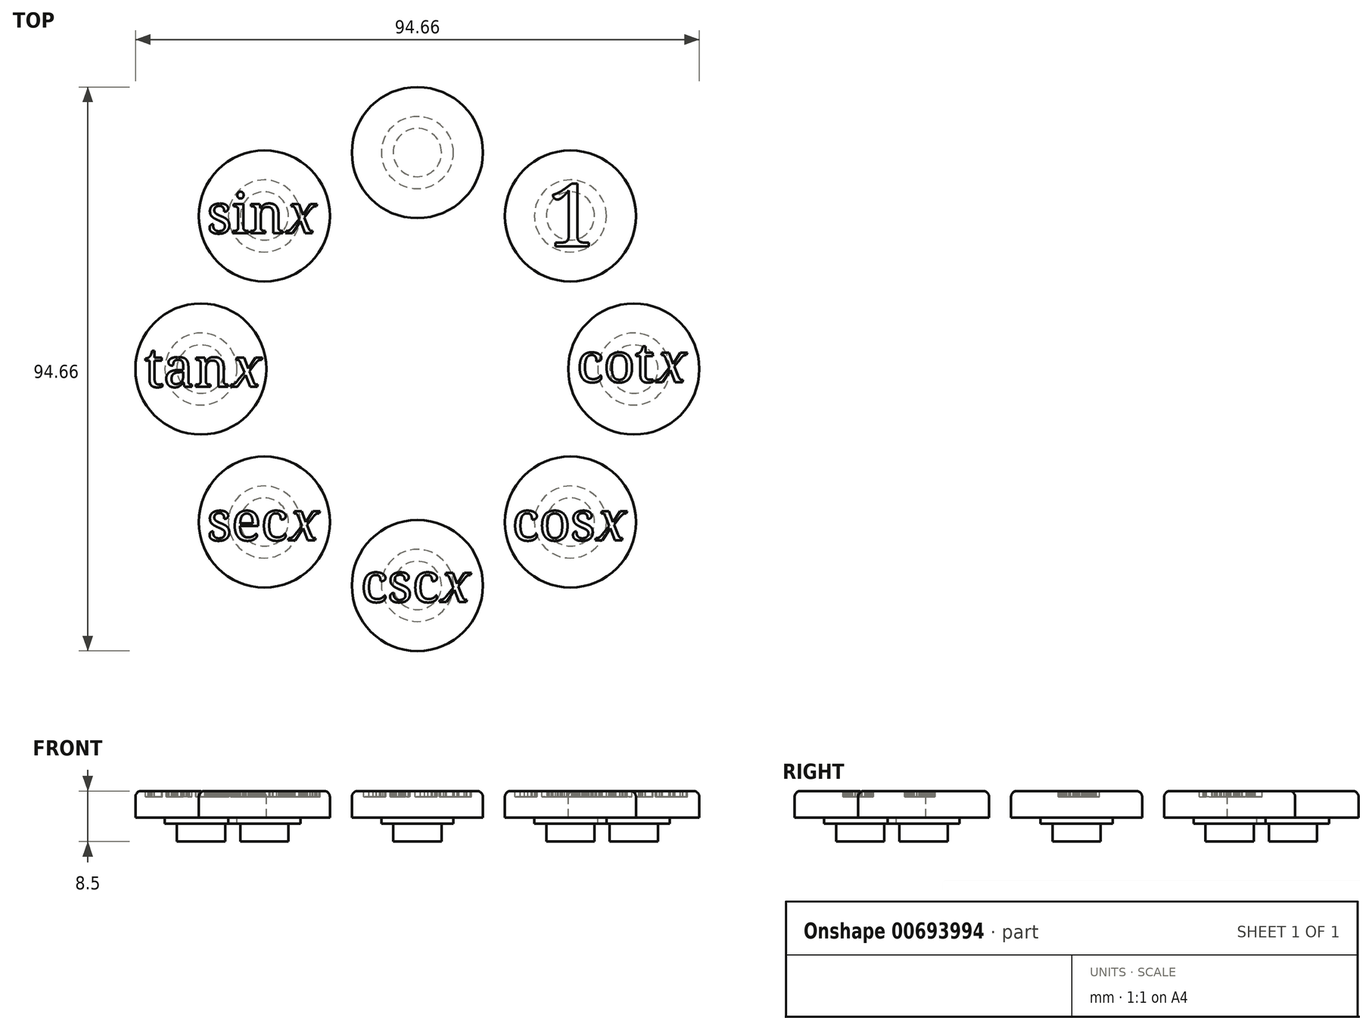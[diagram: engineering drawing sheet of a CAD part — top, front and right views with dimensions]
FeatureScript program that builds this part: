
annotation { "Feature Type Name" : "Feature", "Feature Type Description" : "" }
export const myFeature = defineFeature(function(context is Context, id is Id, definition is map)
    precondition{}
    {
        {
            var Q0;
            Q0=qCreatedBy(makeId("Top.planeOp"),FACE);
            var sketch = newSketch(context, id + "F0", { "sketchPlane" : qUnion([Q0])});
            skCircle(sketch, "E0", {"center": v(0, 0) * mm, "radius": 11 * mm});
            skCircle(sketch, "E1.0", {"center": v(0, 0) * mm, "radius": 4.05 * mm});
            skCircle(sketch, "E2.0", {"center": v(0, 0) * mm, "radius": 6.05 * mm});
            skSolve(sketch);
        }
        {
            var Q0;
            Q0=makeQuery(id+"F0.imprint","IMPRINT",FACE,{"disambiguationData":[TD([[makeQuery(id+"F0.imprint","IMPRINT",EDGE,{"derivedFrom":sQuery(id+"F0.wireOp",EDGE,"E0")}),1.0]])]});
            extrude(context, id + "F1", {"entities" : qUnion([Q0]), "depth" : 4.5 * mm, "offsetDistance" : 25.4 * mm});
        }
        {
            var Q0;
            Q0=makeQuery(id+"F0.imprint","IMPRINT",FACE,{"disambiguationData":[TD([[makeQuery(id+"F0.imprint","IMPRINT",EDGE,{"derivedFrom":sQuery(id+"F0.wireOp",EDGE,"E1.0")}),1.0]])]});
            var Q1;
            Q1=makeQuery(id+"F0.imprint","IMPRINT",FACE,{"disambiguationData":[TD([[makeQuery(id+"F0.imprint","IMPRINT",EDGE,{"derivedFrom":sQuery(id+"F0.wireOp",EDGE,"E1.0")}),-1.0]])]});
            extrude(context, id + "F2", {"entities" : qUnion([Q0, Q1]), "operationType" : NewBodyOperationType.ADD, "depth" : 5.5 * mm, "offsetDistance" : 25.4 * mm});
        }
        {
            var Q0;
            Q0=makeQuery(id+"F0.imprint","IMPRINT",FACE,{"disambiguationData":[TD([[makeQuery(id+"F0.imprint","IMPRINT",EDGE,{"derivedFrom":sQuery(id+"F0.wireOp",EDGE,"E1.0")}),1.0]])]});
            extrude(context, id + "F3", {"entities" : qUnion([Q0]), "operationType" : NewBodyOperationType.ADD, "depth" : 8.5 * mm, "offsetDistance" : 25.4 * mm});
        }
        {
            var Q0;
            Q0=makeQuery(id+"F1.opExtrude","CAP_EDGE",EDGE,{"disambiguationData":[OSD([sQuery(id+"F0.wireOp",EDGE,"E0")])],"isStart":true});
            fillet(context, id + "F4", {"entities" : qUnion([Q0]), "radius" : 1.02 * mm, "tangentPropagation" : true, "allowEdgeOverflow" : false});
        }
        {
            var Q0;
            Q0=qCreatedBy(makeId("Right.planeOp"),FACE);
            var sketch = newSketch(context, id + "F5", { "sketchPlane" : qUnion([Q0])});
            skLineSegment(sketch, "E3", {"start": v(-36.33, -6.15) * mm, "end": v(-36.33, 36.38) * mm});
            skLineSegment(sketch, "E4", {"start": v(0, 0) * mm, "end": v(-88.4, 0) * mm});
            skSolve(sketch);
        }
        {
            var Q0;
            Q0=makeQuery(id+"F1.opExtrude","SWEPT_BODY",BODY,{"disambiguationData":[OSD([sQuery(id+"F0.wireOp",EDGE,"E0"),sQuery(id+"F0.wireOp",EDGE,"E2.0")])]});
            var Q1;
            Q1=sQuery(id+"F5.wireOp",EDGE,"E3");
            circularPattern(context, id + "F6", {"entities" : qUnion([Q0]), "axis" : qUnion([Q1]), "angle" : 360 * degree, "instanceCount" : 8, "equalSpace" : true});
        }
        {
            var Q0;
            Q0=makeQuery(id+"F6.opPattern","COPY",BODY,{"derivedFrom":makeQuery(id+"F1.opExtrude","SWEPT_BODY",BODY,{"disambiguationData":[OSD([sQuery(id+"F0.wireOp",EDGE,"E0"),sQuery(id+"F0.wireOp",EDGE,"E2.0")])]}),"instanceName":"7"});
            var Q1;
            Q1=makeQuery(id+"F1.opExtrude","SWEPT_BODY",BODY,{"disambiguationData":[OSD([sQuery(id+"F0.wireOp",EDGE,"E0"),sQuery(id+"F0.wireOp",EDGE,"E2.0")])]});
            var Q2;
            Q2=makeQuery(id+"F6.opPattern","COPY",BODY,{"derivedFrom":makeQuery(id+"F1.opExtrude","SWEPT_BODY",BODY,{"disambiguationData":[OSD([sQuery(id+"F0.wireOp",EDGE,"E0"),sQuery(id+"F0.wireOp",EDGE,"E2.0")])]}),"instanceName":"1"});
            var Q3;
            Q3=makeQuery(id+"F6.opPattern","COPY",BODY,{"derivedFrom":makeQuery(id+"F1.opExtrude","SWEPT_BODY",BODY,{"disambiguationData":[OSD([sQuery(id+"F0.wireOp",EDGE,"E0"),sQuery(id+"F0.wireOp",EDGE,"E2.0")])]}),"instanceName":"2"});
            var Q4;
            Q4=makeQuery(id+"F6.opPattern","COPY",BODY,{"derivedFrom":makeQuery(id+"F1.opExtrude","SWEPT_BODY",BODY,{"disambiguationData":[OSD([sQuery(id+"F0.wireOp",EDGE,"E0"),sQuery(id+"F0.wireOp",EDGE,"E2.0")])]}),"instanceName":"3"});
            var Q5;
            Q5=makeQuery(id+"F6.opPattern","COPY",BODY,{"derivedFrom":makeQuery(id+"F1.opExtrude","SWEPT_BODY",BODY,{"disambiguationData":[OSD([sQuery(id+"F0.wireOp",EDGE,"E0"),sQuery(id+"F0.wireOp",EDGE,"E2.0")])]}),"instanceName":"4"});
            var Q6;
            Q6=makeQuery(id+"F6.opPattern","COPY",BODY,{"derivedFrom":makeQuery(id+"F1.opExtrude","SWEPT_BODY",BODY,{"disambiguationData":[OSD([sQuery(id+"F0.wireOp",EDGE,"E0"),sQuery(id+"F0.wireOp",EDGE,"E2.0")])]}),"instanceName":"5"});
            var Q7;
            Q7=makeQuery(id+"F6.opPattern","COPY",BODY,{"derivedFrom":makeQuery(id+"F1.opExtrude","SWEPT_BODY",BODY,{"disambiguationData":[OSD([sQuery(id+"F0.wireOp",EDGE,"E0"),sQuery(id+"F0.wireOp",EDGE,"E2.0")])]}),"instanceName":"6"});
            var Q8;
            Q8=sQuery(id+"F5.wireOp",EDGE,"E4");
            transform(context, id + "F7", {"entities" : qUnion([Q0, Q1, Q2, Q3, Q4, Q5, Q6, Q7]), "transformType" : TransformType.ROTATION, "transformAxis" : qUnion([Q8]), "angle" : 180 * degree, "makeCopy" : false});
        }
        {
            var Q0;
            Q0=qCreatedBy(makeId("Top.planeOp"),FACE);
            var sketch = newSketch(context, id + "F8", { "sketchPlane" : qUnion([Q0])});
            skText(sketch, "E5", { "text": "sin", "fontName": "NotoSerif-Regular.ttf"});
            skText(sketch, "E6", { "text": "x", "fontName": "NotoSerif-Italic.ttf"});
            skText(sketch, "E7", { "text": "tan", "fontName": "NotoSerif-Regular.ttf"});
            skText(sketch, "E8", { "text": "x", "fontName": "NotoSerif-Italic.ttf"});
            skText(sketch, "E9", { "text": "sec", "fontName": "NotoSerif-Regular.ttf"});
            skText(sketch, "E10", { "text": "x", "fontName": "NotoSerif-Italic.ttf"});
            skText(sketch, "E11", { "text": "csc", "fontName": "NotoSerif-Regular.ttf"});
            skText(sketch, "E12", { "text": "x", "fontName": "NotoSerif-Italic.ttf"});
            skText(sketch, "E13", { "text": "cos", "fontName": "NotoSerif-Regular.ttf"});
            skText(sketch, "E14", { "text": "x", "fontName": "NotoSerif-Italic.ttf"});
            skText(sketch, "E15", { "text": "cot", "fontName": "NotoSerif-Regular.ttf"});
            skText(sketch, "E16", { "text": "x", "fontName": "NotoSerif-Italic.ttf"});
            skText(sketch, "E17", { "text": "1", "fontName": "NotoSerif-Regular.ttf"});
            const initialGuessF8  = {"E5": [-0.0353, -0.01354, 1, 0, 0.0066], "E6": [-0.02196, -0.01354, 1, 0, 0.0066], "E7": [-0.04584, -0.03933, 1, 0, 0.0066], "E8": [-0.03119, -0.03933, 1, 0, 0.0066], "E9": [-0.0353, -0.0651, 1, 0, 0.0066], "E10": [-0.0215, -0.0651, 1, 0, 0.0066], "E11": [-0.0095, -0.07545, 1, 0, 0.0066], "E12": [0.0039, -0.07545, 1, 0, 0.0066], "E13": [0.01591, -0.0651, 1, 0, 0.0066], "E14": [0.03005, -0.0651, 1, 0, 0.0066], "E15": [0.02674, -0.03853, 1, 0, 0.0066], "E16": [0.04016, -0.03853, 1, 0, 0.0066], "E17": [0.0218, -0.01572, 1, 0, 0.01055]};
            skSetInitialGuess(sketch, initialGuessF8);
            skSolve(sketch);
        }
        {
            var Q0;
            Q0=qSketchRegion(id+"F8",true);
            extrude(context, id + "F9", {"entities" : qUnion([Q0]), "operationType" : NewBodyOperationType.REMOVE, "oppositeDirection" : true, "depth" : 1 * mm, "offsetDistance" : 25 * mm});
        }
    });
